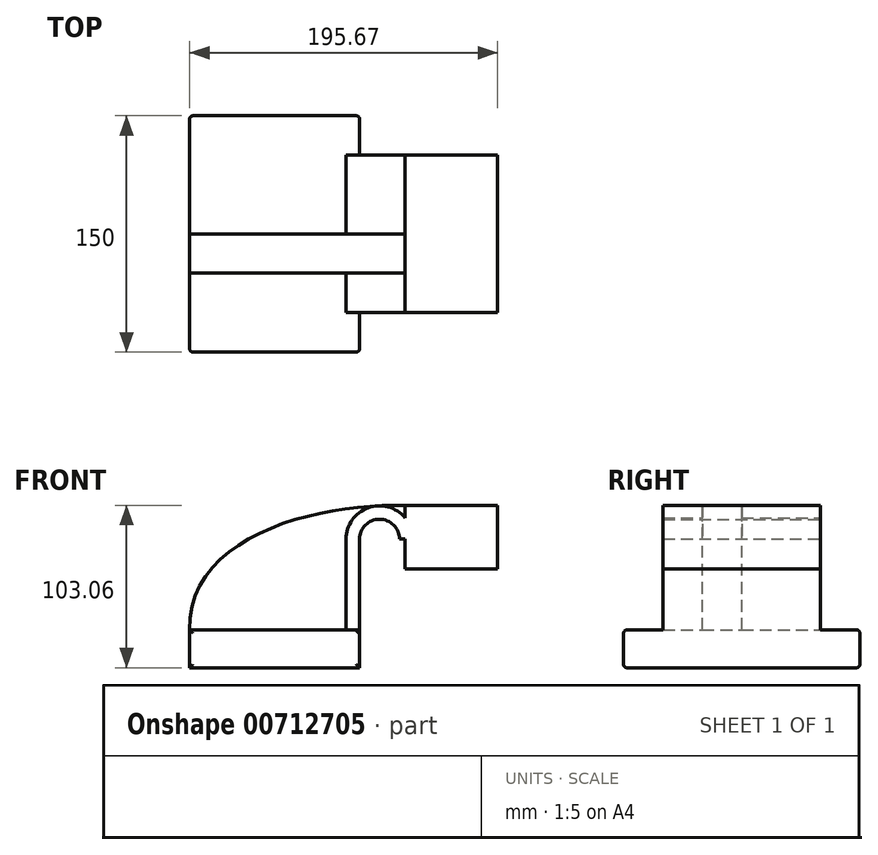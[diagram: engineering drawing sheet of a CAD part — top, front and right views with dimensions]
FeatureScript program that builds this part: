
annotation { "Feature Type Name" : "Feature", "Feature Type Description" : "" }
export const myFeature = defineFeature(function(context is Context, id is Id, definition is map)
    precondition{}
    {
        {
            var Q0;
            Q0=qCreatedBy(makeId("Front.planeOp"),FACE);
            var sketch = newSketch(context, id + "F0", { "sketchPlane" : qUnion([Q0])});
            skLineSegment(sketch, "E0.bottom", {"start": v(-53.96, 12) * mm, "end": v(53.96, 12) * mm});
            skLineSegment(sketch, "E0.top", {"start": v(-53.96, -12) * mm, "end": v(53.96, -12) * mm});
            skLineSegment(sketch, "E0.left", {"start": v(-53.96, 12) * mm, "end": v(-53.96, -12) * mm});
            skLineSegment(sketch, "E0.right", {"start": v(53.96, 12) * mm, "end": v(53.96, -12) * mm});
            skPoint(sketch, "E0.middle", {"position": v(0, 0) * mm});
            skLineSegment(sketch, "E1.bottom", {"start": v(82.9, 50.87) * mm, "end": v(141.7, 50.87) * mm});
            skLineSegment(sketch, "E1.top", {"start": v(82.9, 90.9) * mm, "end": v(141.7, 90.9) * mm});
            skLineSegment(sketch, "E1.left", {"start": v(82.9, 50.87) * mm, "end": v(82.9, 90.9) * mm});
            skLineSegment(sketch, "E1.right", {"start": v(141.7, 50.87) * mm, "end": v(141.7, 90.9) * mm});
            skPoint(sketch, "E1.middle", {"position": v(112.3, 70.89) * mm});
            skLineSegment(sketch, "E2", {"start": v(53.96, 12) * mm, "end": v(53.96, 69.64) * mm});
            skArc(sketch, "E3", {"start": v(53.96, 69.64) * mm, "mid": v(66.63, 82.31) * mm, "end": v(79.3, 69.64) * mm});
            skLineSegment(sketch, "E4", {"start": v(79.3, 69.64) * mm, "end": v(104.51, 69.64) * mm});
            skLineSegment(sketch, "E5.0", {"start": v(86.04, 78.16) * mm, "end": v(104.51, 78.16) * mm});
            skArc(sketch, "E5.1", {"start": v(45.43, 69.64) * mm, "mid": v(62.28, 90.38) * mm, "end": v(86.04, 78.16) * mm});
            skLineSegment(sketch, "E5.2", {"start": v(45.43, 12) * mm, "end": v(45.43, 69.64) * mm});
            skLineSegment(sketch, "E6", {"start": v(98.34, 78.16) * mm, "end": v(98.34, 69.64) * mm});
            skFitSpline(sketch, "E7", {"points": [v(-53.96, 12) * mm, v(82.9, 90.9) * mm], "startDerivative": vector(-4.4, 181.92) * mm, "endDerivative": vector(159.62, -6.55) * mm});
            skSolve(sketch);
        }
        {
            var Q0;
            Q0=makeQuery(id+"F0.imprint","IMPRINT",FACE,{"disambiguationData":[TD([[makeQuery(id+"F0.imprint","IMPRINT",EDGE,{"derivedFrom":sQuery(id+"F0.wireOp",EDGE,"E0.top")}),1.0]])]});
            var sketch = newSketch(context, id + "F1", { "sketchPlane" : qUnion([Q0])});
            skSolve(sketch);
        }
        {
            var Q0;
            {var subQ5=sQuery(id+"F0.wireOp",EDGE,"E6");Q0=makeQuery(id+"F0.imprint","IMPRINT",FACE,{"disambiguationData":[TD([[makeQuery(id+"F0.imprint","IMPRINT",EDGE,{"derivedFrom":subQ5}),-1.0]])]});}
            var Q1;
            {var subQ4=sQuery(id+"F0.wireOp",EDGE,"E1.bottom");Q1=makeQuery(id+"F0.imprint","IMPRINT",FACE,{"disambiguationData":[TD([[makeQuery(id+"F0.imprint","IMPRINT",EDGE,{"derivedFrom":subQ4}),1.0]])]});}
            var Q2;
            {var subQ1=sQuery(id+"F0.wireOp",EDGE,"E2");Q2=makeQuery(id+"F0.imprint","IMPRINT",FACE,{"disambiguationData":[TD([[makeQuery(id+"F0.imprint","IMPRINT",EDGE,{"derivedFrom":subQ1}),1.0]])]});}
            extrude(context, id + "F2", {"entities" : qUnion([Q0, Q1, Q2]), "endBound" : BoundingType.SYMMETRIC, "depth" : 100 * mm, "offsetDistance" : 25 * mm});
        }
        {
            var Q0;
            Q0 = qSketchRegion(id + "F0", true);
            extrude(context, id + "F3", {"entities" : qUnion([Q0]), "operationType" : NewBodyOperationType.ADD, "depth" : 25 * mm, "offsetDistance" : 25 * mm});
        }
        {
            var Q0;
            Q0=makeQuery(id+"F0.imprint","IMPRINT",FACE,{"disambiguationData":[TD([[makeQuery(id+"F0.imprint","IMPRINT",EDGE,{"derivedFrom":sQuery(id+"F0.wireOp",EDGE,"E0.top")}),1.0]])]});
            extrude(context, id + "F4", {"entities" : qUnion([Q0]), "operationType" : NewBodyOperationType.ADD, "endBound" : BoundingType.SYMMETRIC, "depth" : 50 * mm, "offsetDistance" : 25 * mm});
        }
        {
            var Q0;
            Q0=makeQuery(id+"F2.opExtrude","CAP_EDGE",EDGE,{"disambiguationData":[OSD([sQuery(id+"F0.wireOp",EDGE,"E1.right")])],"isStart":true});
            var Q1;
            Q1=sQuery(id+"F0.wireOp",EDGE,"E1.right");
            revolve(context, id + "F5", {"bodyType" : ToolBodyType.SURFACE, "operationType" : NewBodyOperationType.ADD, "surfaceOperationType" : NewSurfaceOperationType.NEW, "surfaceEntities" : qUnion([Q0]), "axis" : qUnion([Q1]), "revolveType" : RevolveType.FULL});
        }
        {
            var Q0;
            Q0=makeQuery(id+"F1.imprint","IMPRINT",FACE,{"disambiguationData":[TD([[makeQuery(id+"F1.imprint","IMPRINT",EDGE,{"derivedFrom":makeQuery(id+"F0.imprint","IMPRINT",EDGE,{"derivedFrom":sQuery(id+"F0.wireOp",EDGE,"E0.top")})}),1.0]])]});
            extrude(context, id + "F6", {"entities" : qUnion([Q0]), "operationType" : NewBodyOperationType.ADD, "endBound" : BoundingType.SYMMETRIC, "depth" : 150 * mm, "offsetDistance" : 25 * mm});
        }
        {
            var Q0;
            Q0=makeQuery(id+"F6.opExtrude","CAP_FACE",FACE,{"disambiguationData":[OSD([sQuery(id+"F0.wireOp",EDGE,"E0.bottom"),sQuery(id+"F0.wireOp",EDGE,"E0.top"),sQuery(id+"F0.wireOp",EDGE,"E0.left"),sQuery(id+"F0.wireOp",EDGE,"E0.right")])],"isStart":false});
            var Q1;
            Q1=makeQuery(id+"F6.opExtrude","CAP_FACE",FACE,{"disambiguationData":[OSD([sQuery(id+"F0.wireOp",EDGE,"E0.bottom"),sQuery(id+"F0.wireOp",EDGE,"E0.top"),sQuery(id+"F0.wireOp",EDGE,"E0.left"),sQuery(id+"F0.wireOp",EDGE,"E0.right")])],"isStart":true});
            fillet(context, id + "F7", {"entities" : qUnion([Q0, Q1]), "radius" : 2 * mm, "tangentPropagation" : true, "allowEdgeOverflow" : false});
        }
    });
